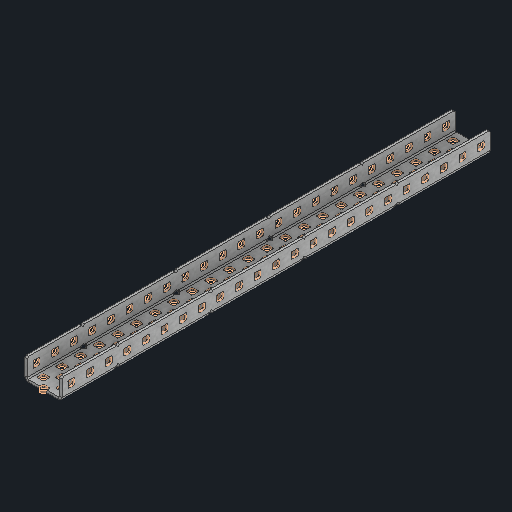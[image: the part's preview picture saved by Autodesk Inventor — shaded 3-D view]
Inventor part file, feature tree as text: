
AUTODESK INVENTOR PART (.ipt)
format: ipt  version: 2025 (Build 290162000, 162)  size: 1,942,016 bytes
history: native  units: in
note: dims shown in document units (in); Inventor stores cm internally (conversion verified against a paired STEP export)
features: other x236, sketch x5, sheet_metal_op x1
ambient origin geometry x8: Origin, YZ Plane, XZ Plane, XY Plane, X Axis, Y Axis, Z Axis, Center Point
bodies: Solid1 (feature_tree)
feature tree (242):
  other  "Alu C 1x2x1x23.ipt"
  other  "Solid1::Alu C 1x2x1x23.ipt"
  other  "TaggingFeature1"
  sketch  "Sketch1"  dims[d0=0.3937in]
  sketch  "Sketch2"  dims[d1=0.0625in]
  sketch  "Sketch3"
  other  "Flange Pattern Sketch"
  sketch  "Sketch9"
  sheet_metal_op  "Body Pattern Sketch"
  other  "Arc Length"
  sketch  "Sketch14"
  other  "Flange Pattern Plane"
  other  "Srf1"
  other  "Srf2"
  other  "Srf3"
  other  "Srf4"
  other  "Srf5"
  other  "Srf6"
  other  "Srf7"
  other  "Srf8"
  other  "Srf9"
  other  "Srf10"
  other  "Srf11"
  other  "Srf12"
  other  "Srf13"
  other  "Srf14"
  other  "Srf15"
  other  "Srf16"
  other  "Srf17"
  other  "Srf18"
  other  "Srf19"
  other  "Srf20"
  other  "Srf21"
  other  "Srf22"
  other  "Srf23"
  other  "Srf24"
  other  "Srf25"
  other  "Srf26"
  other  "Srf27"
  other  "Srf28"
  other  "Srf29"
  other  "Srf30"
  other  "Srf31"
  other  "Srf32"
  other  "Srf33"
  other  "Srf34"
  other  "Srf35"
  other  "Srf36"
  other  "Srf37"
  other  "Srf38"
  other  "Srf39"
  other  "Srf40"
  other  "Srf41"
  other  "Srf42"
  other  "Srf43"
  other  "Srf44"
  other  "Srf45"
  other  "Srf46"
  other  "Srf47"
  other  "Srf48"
  other  "Srf49"
  other  "Srf50"
  other  "Srf51"
  other  "Srf52"
  other  "Srf53"
  other  "Srf54"
  other  "Srf55"
  other  "Srf56"
  other  "Srf57"
  other  "Srf58"
  other  "Srf59"
  other  "Srf60"
  other  "Srf61"
  other  "Srf62"
  other  "Srf63"
  other  "Srf64"
  other  "Srf65"
  other  "Srf66"
  other  "Srf67"
  other  "Srf68"
  other  "Srf69"
  other  "Srf70"
  other  "Srf71"
  other  "Srf72"
  other  "Srf73"
  other  "Srf74"
  other  "Srf75"
  other  "Srf76"
  other  "Srf77"
  other  "Srf78"
  other  "Srf79"
  other  "Srf80"
  other  "Srf81"
  other  "Srf82"
  other  "Srf83"
  other  "Srf84"
  other  "Srf85"
  other  "Srf86"
  other  "Srf87"
  other  "Srf88"
  other  "Srf89"
  other  "Srf90"
  other  "Srf91"
  other  "Srf92"
  other  "Srf93"
  other  "Srf94"
  other  "Srf95"
  other  "Srf96"
  other  "Srf97"
  other  "Srf98"
  other  "Srf99"
  other  "Srf100"
  other  "Srf101"
  other  "Srf102"
  other  "Srf103"
  other  "Srf104"
  other  "Srf105"
  other  "Srf106"
  other  "Srf107"
  other  "Srf108"
  other  "Srf109"
  other  "Srf110"
  other  "Srf111"
  other  "Srf112"
  other  "Srf113"
  other  "Srf114"
  other  "Srf115"
  other  "Srf1::Derived"
  other  "Srf2::Derived"
  other  "Srf823::Derived"
  other  "Srf824::Derived"
  other  "Srf825::Derived"
  other  "Srf826::Derived"
  other  "Srf827::Derived"
  other  "Srf828::Derived"
  other  "Srf829::Derived"
  other  "Srf922::Derived"
  other  "Srf923::Derived"
  other  "Srf924::Derived"
  other  "Srf925::Derived"
  other  "Srf926::Derived"
  other  "Srf1143::Derived"
  other  "Srf1144::Derived"
  other  "Srf1145::Derived"
  other  "Srf1146::Derived"
  other  "Srf1147::Derived"
  other  "Srf1148::Derived"
  other  "Srf1149::Derived"
  other  "Srf1150::Derived"
  other  "Srf1151::Derived"
  other  "Srf1152::Derived"
  other  "Srf1153::Derived"
  other  "Srf1154::Derived"
  other  "Srf1155::Derived"
  other  "Srf1156::Derived"
  other  "Srf1157::Derived"
  other  "Srf1158::Derived"
  other  "Srf1159::Derived"
  other  "Srf1160::Derived"
  other  "Srf1161::Derived"
  other  "Srf1162::Derived"
  other  "Srf1163::Derived"
  other  "Srf1164::Derived"
  other  "Srf1165::Derived"
  other  "Srf1166::Derived"
  other  "Srf1167::Derived"
  other  "Srf1168::Derived"
  other  "Srf1169::Derived"
  other  "Srf1170::Derived"
  other  "Srf1171::Derived"
  other  "Srf1172::Derived"
  other  "Srf1173::Derived"
  other  "Srf1174::Derived"
  other  "Srf91::Derived"
  other  "Srf92::Derived"
  other  "Srf856::Derived"
  other  "Srf857::Derived"
  other  "Srf858::Derived"
  other  "Srf859::Derived"
  other  "Srf860::Derived"
  other  "Srf861::Derived"
  other  "Srf862::Derived"
  other  "Srf959::Derived"
  other  "Srf960::Derived"
  other  "Srf961::Derived"
  other  "Srf962::Derived"
  other  "Srf963::Derived"
  other  "Srf1199::Derived"
  other  "Srf1200::Derived"
  other  "Srf1201::Derived"
  other  "Srf1202::Derived"
  other  "Srf1203::Derived"
  other  "Srf1204::Derived"
  other  "Srf1205::Derived"
  other  "Srf1206::Derived"
  other  "Srf1207::Derived"
  other  "Srf1208::Derived"
  other  "Srf1209::Derived"
  other  "Srf1210::Derived"
  other  "Srf1211::Derived"
  other  "Srf1212::Derived"
  other  "Srf1213::Derived"
  other  "Srf1214::Derived"
  other  "Srf1215::Derived"
  other  "Srf1216::Derived"
  other  "Srf1217::Derived"
  other  "Srf1218::Derived"
  other  "Srf1219::Derived"
  other  "Srf1220::Derived"
  other  "Srf1221::Derived"
  other  "Srf1222::Derived"
  other  "Srf1223::Derived"
  other  "Srf1224::Derived"
  other  "Srf1225::Derived"
  other  "Srf1226::Derived"
  other  "Srf1227::Derived"
  other  "Srf1228::Derived"
  other  "Srf1229::Derived"
  other  "Srf1230::Derived"
  other  "Srf786::Derived"
  other  "Srf889::Derived"
  other  "Srf890::Derived"
  other  "Srf891::Derived"
  other  "Srf892::Derived"
  other  "Srf893::Derived"
  other  "Srf894::Derived"
  other  "Srf895::Derived"
  other  "Srf896::Derived"
  other  "Srf996::Derived"
  other  "Srf997::Derived"
  other  "Srf998::Derived"
  other  "Srf999::Derived"
  other  "Srf1000::Derived"
  other  "Srf1255::Derived"
  other  "Srf1256::Derived"
  other  "Srf1257::Derived"
  other  "Srf1258::Derived"
  other  "Srf1259::Derived"
  other  "Srf1260::Derived"
  other  "Srf1261::Derived"
  other  "Srf1262::Derived"
  other  "Srf1263::Derived"
